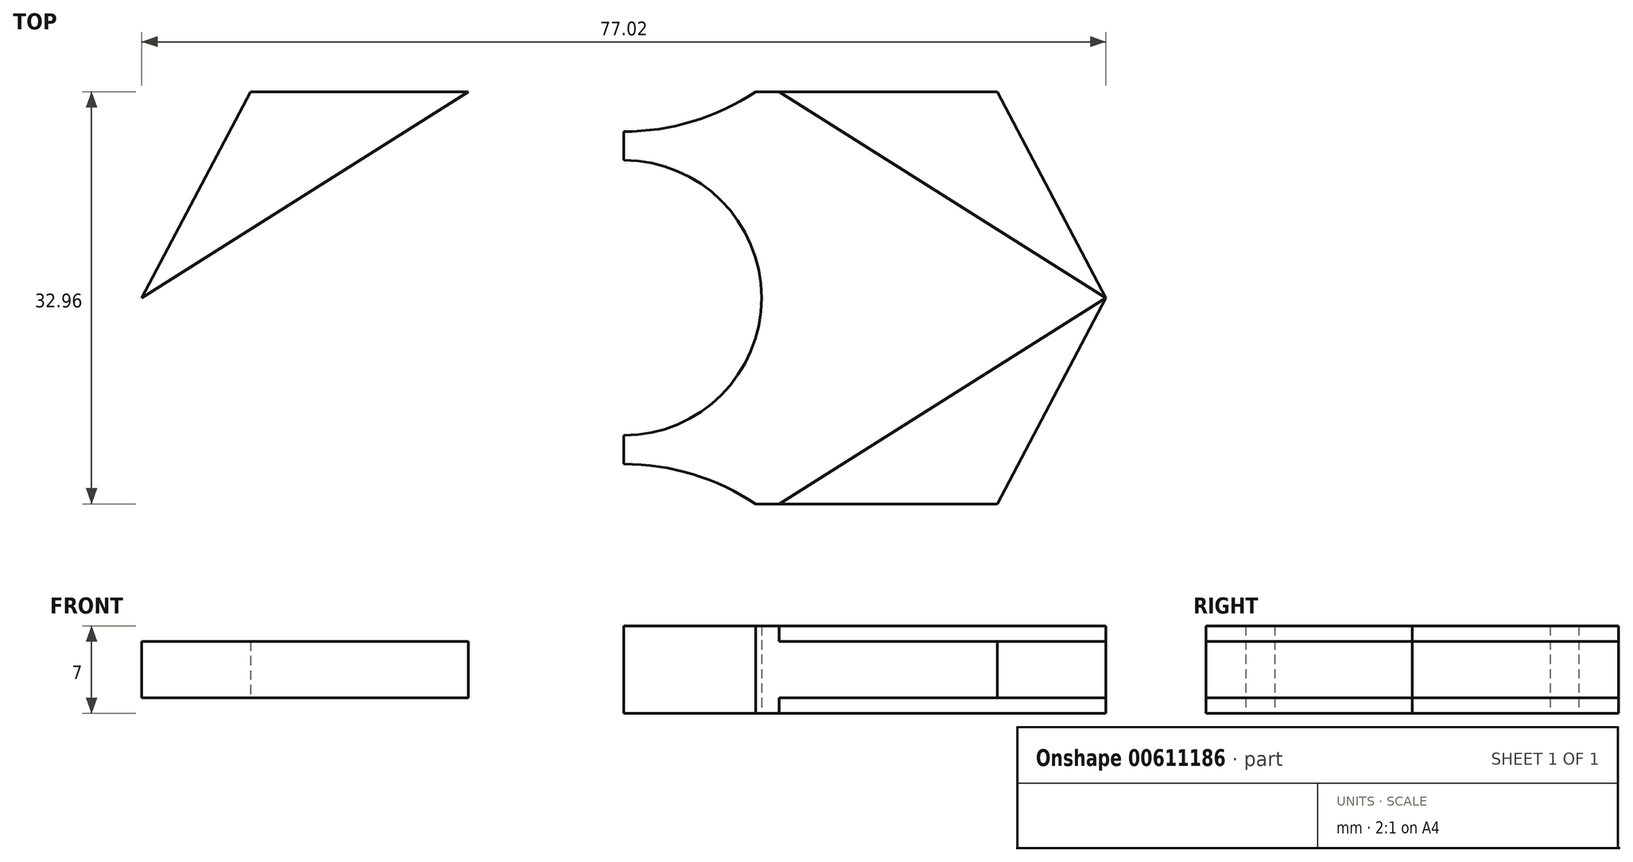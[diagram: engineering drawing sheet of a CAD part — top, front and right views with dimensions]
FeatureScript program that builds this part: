
annotation { "Feature Type Name" : "Feature", "Feature Type Description" : "" }
export const myFeature = defineFeature(function(context is Context, id is Id, definition is map)
    precondition{}
    {
        {
            var Q0;
            Q0=qCreatedBy(makeId("Top.planeOp"),FACE);
            var sketch = newSketch(context, id + "F0", { "sketchPlane" : qUnion([Q0])});
            skLineSegment(sketch, "E0.bottom", {"start": v(38.54, 16.48) * mm, "end": v(-38.54, 16.48) * mm});
            skLineSegment(sketch, "E0.top", {"start": v(38.54, -16.48) * mm, "end": v(-38.54, -16.48) * mm});
            skLineSegment(sketch, "E0.left", {"start": v(38.54, 16.48) * mm, "end": v(38.54, -16.48) * mm});
            skLineSegment(sketch, "E0.right", {"start": v(-38.54, 16.48) * mm, "end": v(-38.54, -16.48) * mm});
            skPoint(sketch, "E0.middle", {"position": v(0, 0) * mm});
            skLineSegment(sketch, "E1.left", {"start": v(38.54, 7.18) * mm, "end": v(38.48, -7.18) * mm});
            skLineSegment(sketch, "E1.right", {"start": v(-38.48, 7.18) * mm, "end": v(-38.54, -7.18) * mm});
            skLineSegment(sketch, "E2", {"start": v(-38.5, 0) * mm, "end": v(-12.42, -16.48) * mm});
            skLineSegment(sketch, "E3", {"start": v(-12.42, -16.48) * mm, "end": v(-38.5, 0) * mm});
            skLineSegment(sketch, "E4", {"start": v(-38.5, 0) * mm, "end": v(-12.42, 16.48) * mm});
            skLineSegment(sketch, "E5.MirrorCS", {"start": v(38.5, 0) * mm, "end": v(12.42, -16.48) * mm});
            skLineSegment(sketch, "E6.MirrorCS", {"start": v(38.5, 0) * mm, "end": v(12.42, 16.48) * mm});
            skLineSegment(sketch, "E7", {"start": v(-38.5, 0) * mm, "end": v(-29.83, 16.48) * mm});
            skLineSegment(sketch, "E8", {"start": v(-38.5, 0) * mm, "end": v(-29.83, -16.48) * mm});
            skLineSegment(sketch, "E9.MirrorCS", {"start": v(38.5, 0) * mm, "end": v(29.83, 16.48) * mm});
            skLineSegment(sketch, "E10.MirrorCS", {"start": v(38.5, 0) * mm, "end": v(29.83, -16.48) * mm});
            skLineSegment(sketch, "E11", {"start": v(0, 0) * mm, "end": v(0, 32.3) * mm});
            skPoint(sketch, "E11.endSnap0", {"position": v(0, 16.48) * mm});
            skCircle(sketch, "E12", {"center": v(0, 32.3) * mm, "radius": 19 * mm});
            skCircle(sketch, "E13.MirrorC", {"center": v(0, -32.3) * mm, "radius": 19 * mm});
            skLineSegment(sketch, "E14.MirrorCS", {"start": v(0, 0) * mm, "end": v(0, -32.3) * mm});
            skCircle(sketch, "E15", {"center": v(0, 0) * mm, "radius": 11 * mm});
            skSolve(sketch);
        }
        {
            var Q0;
            {var subQ0=sQuery(id+"F0.wireOp",EDGE,"E3");Q0=makeQuery(id+"F0.imprint","IMPRINT",FACE,{"disambiguationData":[TD([[makeQuery(id+"F0.imprint","IMPRINT",EDGE,{"derivedFrom":subQ0}),-1.0]])]});}
            var Q1;
            {var subQ0=sQuery(id+"F0.wireOp",EDGE,"E5.MirrorCS");Q1=makeQuery(id+"F0.imprint","IMPRINT",FACE,{"disambiguationData":[TD([[makeQuery(id+"F0.imprint","IMPRINT",EDGE,{"derivedFrom":subQ0}),-1.0]])]});}
            extrude(context, id + "F1", {"entities" : qUnion([Q0, Q1]), "endBound" : BoundingType.SYMMETRIC, "depth" : 7 * mm, "offsetDistance" : 25.4 * mm});
        }
        {
            var Q0;
            {var subQ0=sQuery(id+"F0.wireOp",EDGE,"E5.MirrorCS");Q0=makeQuery(id+"F0.imprint","IMPRINT",FACE,{"disambiguationData":[TD([[makeQuery(id+"F0.imprint","IMPRINT",EDGE,{"derivedFrom":subQ0}),1.0]])]});}
            var Q1;
            {var subQ0=sQuery(id+"F0.wireOp",EDGE,"E6.MirrorCS");Q1=makeQuery(id+"F0.imprint","IMPRINT",FACE,{"disambiguationData":[TD([[makeQuery(id+"F0.imprint","IMPRINT",EDGE,{"derivedFrom":subQ0}),-1.0]])]});}
            var Q2;
            {var subQ0=sQuery(id+"F0.wireOp",EDGE,"E3");Q2=makeQuery(id+"F0.imprint","IMPRINT",FACE,{"disambiguationData":[TD([[makeQuery(id+"F0.imprint","IMPRINT",EDGE,{"derivedFrom":subQ0}),1.0]])]});}
            var Q3;
            {var subQ0=sQuery(id+"F0.wireOp",EDGE,"E4");Q3=makeQuery(id+"F0.imprint","IMPRINT",FACE,{"disambiguationData":[TD([[makeQuery(id+"F0.imprint","IMPRINT",EDGE,{"derivedFrom":subQ0}),1.0]])]});}
            extrude(context, id + "F2", {"entities" : qUnion([Q0, Q1, Q2, Q3]), "operationType" : NewBodyOperationType.ADD, "endBound" : BoundingType.SYMMETRIC, "depth" : 4.5 * mm, "offsetDistance" : 25.4 * mm});
        }
    });
